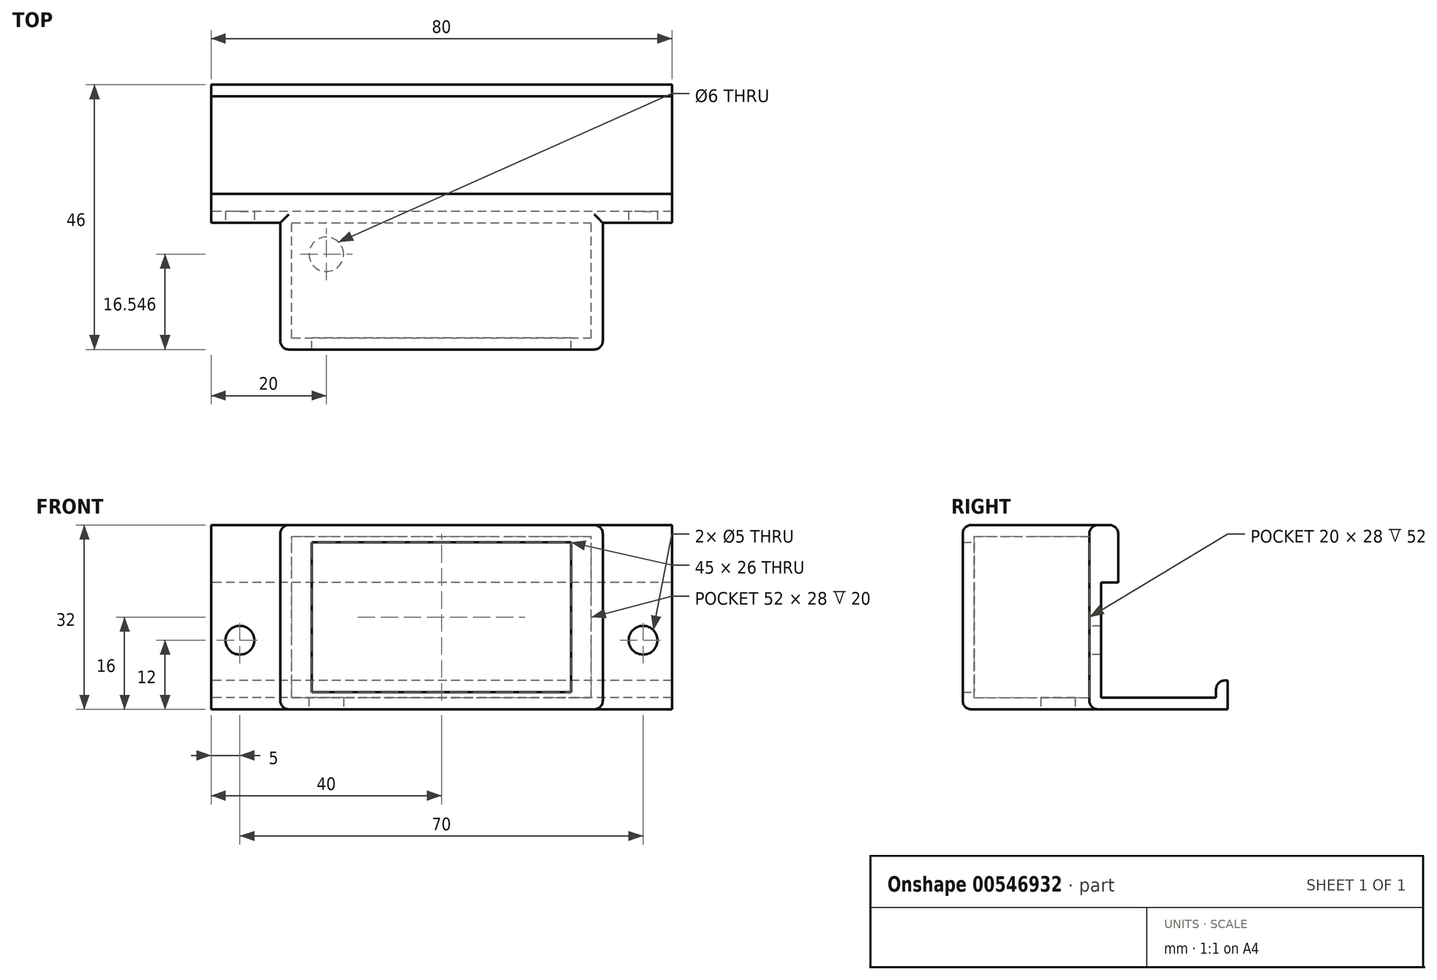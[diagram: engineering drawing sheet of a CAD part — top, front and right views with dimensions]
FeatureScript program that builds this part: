
annotation { "Feature Type Name" : "Feature", "Feature Type Description" : "" }
export const myFeature = defineFeature(function(context is Context, id is Id, definition is map)
    precondition{}
    {
        {
            var Q0;
            Q0=qCreatedBy(makeId("Right.planeOp"),FACE);
            var sketch = newSketch(context, id + "F0", { "sketchPlane" : qUnion([Q0])});
            skLineSegment(sketch, "E0", {"start": v(0, 0) * mm, "end": v(0, 32) * mm});
            skLineSegment(sketch, "E1", {"start": v(5, 32) * mm, "end": v(5, 22) * mm});
            skLineSegment(sketch, "E2", {"start": v(5, 22) * mm, "end": v(2, 22) * mm});
            skLineSegment(sketch, "E3", {"start": v(2, 22) * mm, "end": v(2, 2) * mm});
            skLineSegment(sketch, "E4", {"start": v(2, 2) * mm, "end": v(22, 2) * mm});
            skLineSegment(sketch, "E5", {"start": v(22, 2) * mm, "end": v(22, 5) * mm});
            skLineSegment(sketch, "E6", {"start": v(22, 5) * mm, "end": v(24, 5) * mm});
            skLineSegment(sketch, "E7", {"start": v(24, 5) * mm, "end": v(24, 0) * mm});
            skLineSegment(sketch, "E8", {"start": v(24, 0) * mm, "end": v(0, 0) * mm});
            skLineSegment(sketch, "E9.0", {"start": v(0, 32) * mm, "end": v(5, 32) * mm});
            skSolve(sketch);
        }
        {
            var Q0;
            Q0=makeQuery(id+"F0.imprint","IMPRINT",FACE,{"disambiguationData":[TD([[makeQuery(id+"F0.imprint","IMPRINT",EDGE,{"derivedFrom":sQuery(id+"F0.wireOp",EDGE,"E0")}),-1.0]])]});
            extrude(context, id + "F1", {"entities" : qUnion([Q0]), "depth" : 80 * mm, "offsetDistance" : 25 * mm});
        }
        {
            var Q0;
            Q0=qCreatedBy(makeId("Front.planeOp"),FACE);
            var sketch = newSketch(context, id + "F2", { "sketchPlane" : qUnion([Q0])});
            skLineSegment(sketch, "E10", {"start": v(0, 0) * mm, "end": v(0, 12) * mm, "construction": true});
            skLineSegment(sketch, "E11.0", {"start": v(5, 0) * mm, "end": v(5, 12) * mm, "construction": true});
            skCircle(sketch, "E12", {"center": v(5, 12) * mm, "radius": 2.5 * mm});
            skLineSegment(sketch, "E13", {"start": v(0, 0) * mm, "end": v(0, 16) * mm, "construction": true});
            skLineSegment(sketch, "E14", {"start": v(0, 0) * mm, "end": v(0, 32) * mm, "construction": true});
            skLineSegment(sketch, "E15", {"start": v(12, 32) * mm, "end": v(68, 32) * mm});
            skLineSegment(sketch, "E16", {"start": v(12, 0) * mm, "end": v(68, 0) * mm});
            skLineSegment(sketch, "E17", {"start": v(0, 12) * mm, "end": v(80, 12) * mm, "construction": true});
            skLineSegment(sketch, "E18", {"start": v(80, 12) * mm, "end": v(80, 0) * mm, "construction": true});
            skLineSegment(sketch, "E19.0", {"start": v(75, 12) * mm, "end": v(75, 0) * mm, "construction": true});
            skCircle(sketch, "E20", {"center": v(75, 12) * mm, "radius": 2.5 * mm});
            skLineSegment(sketch, "E21.0", {"start": v(40, 0) * mm, "end": v(40, 32) * mm, "construction": true});
            skLineSegment(sketch, "E22.0", {"start": v(68, 0) * mm, "end": v(68, 32) * mm});
            skLineSegment(sketch, "E23.0", {"start": v(12, 0) * mm, "end": v(12, 32) * mm});
            skLineSegment(sketch, "E24.0", {"start": v(14, 30) * mm, "end": v(66, 30) * mm});
            skLineSegment(sketch, "E25.0", {"start": v(14, 2) * mm, "end": v(66, 2) * mm});
            skLineSegment(sketch, "E26.0", {"start": v(14, 2) * mm, "end": v(14, 30) * mm});
            skLineSegment(sketch, "E27.0", {"start": v(66, 2) * mm, "end": v(66, 30) * mm});
            skSolve(sketch);
        }
        {
            var Q0;
            Q0=makeQuery(id+"F2.imprint","IMPRINT",FACE,{"disambiguationData":[TD([[makeQuery(id+"F2.imprint","IMPRINT",EDGE,{"derivedFrom":sQuery(id+"F2.wireOp",EDGE,"E12")}),1.0]])]});
            var Q1;
            Q1=makeQuery(id+"F2.imprint","IMPRINT",FACE,{"disambiguationData":[TD([[makeQuery(id+"F2.imprint","IMPRINT",EDGE,{"derivedFrom":sQuery(id+"F2.wireOp",EDGE,"E20")}),1.0]])]});
            extrude(context, id + "F3", {"entities" : qUnion([Q0, Q1]), "operationType" : NewBodyOperationType.REMOVE, "oppositeDirection" : true, "depth" : 10 * mm, "offsetDistance" : 25 * mm});
        }
        {
            var Q0;
            Q0=makeQuery(id+"F2.imprint","IMPRINT",FACE,{"disambiguationData":[TD([[makeQuery(id+"F2.imprint","IMPRINT",EDGE,{"derivedFrom":sQuery(id+"F2.wireOp",EDGE,"E15")}),-1.0]])]});
            extrude(context, id + "F4", {"entities" : qUnion([Q0]), "operationType" : NewBodyOperationType.ADD, "depth" : 20 * mm, "offsetDistance" : 25 * mm});
        }
        {
            var Q0;
            Q0=qCreatedBy(makeId("Front.planeOp"),FACE);
            cPlane(context, id + "F5", {"entities" : qUnion([Q0]), "cplaneType" : CPlaneType.OFFSET, "offset" : 20 * mm, "width" : 150 * mm, "height" : 150 * mm});
        }
        {
            var Q0;
            Q0=qCreatedBy(id+"F5.planeOp",FACE);
            var sketch = newSketch(context, id + "F6", { "sketchPlane" : qUnion([Q0])});
            skLineSegment(sketch, "E28", {"start": v(12, 0) * mm, "end": v(68, 0) * mm});
            skLineSegment(sketch, "E29", {"start": v(68, 0) * mm, "end": v(68, 32) * mm});
            skLineSegment(sketch, "E30", {"start": v(68, 32) * mm, "end": v(12, 32) * mm});
            skLineSegment(sketch, "E31", {"start": v(12, 32) * mm, "end": v(12, 0) * mm});
            skLineSegment(sketch, "E32.0", {"start": v(62.5, 29) * mm, "end": v(17.5, 29) * mm});
            skLineSegment(sketch, "E33.0", {"start": v(17.5, 3) * mm, "end": v(62.5, 3) * mm});
            skLineSegment(sketch, "E34.0", {"start": v(17.5, 29) * mm, "end": v(17.5, 3) * mm});
            skLineSegment(sketch, "E35.0", {"start": v(62.5, 3) * mm, "end": v(62.5, 29) * mm});
            skSolve(sketch);
        }
        {
            var Q0;
            Q0=makeQuery(id+"F6.imprint","IMPRINT",FACE,{"disambiguationData":[TD([[makeQuery(id+"F6.imprint","IMPRINT",EDGE,{"derivedFrom":sQuery(id+"F6.wireOp",EDGE,"E28")}),1.0]])]});
            extrude(context, id + "F7", {"entities" : qUnion([Q0]), "operationType" : NewBodyOperationType.ADD, "depth" : 2 * mm, "offsetDistance" : 25 * mm});
        }
        {
            var Q0;
            Q0=makeQuery(id+"F7.opExtrude","CAP_EDGE",EDGE,{"disambiguationData":[OSD([sQuery(id+"F6.wireOp",EDGE,"E29")])],"isStart":false});
            var Q1;
            Q1=makeQuery(id+"F7.opExtrude","CAP_EDGE",EDGE,{"disambiguationData":[OSD([sQuery(id+"F6.wireOp",EDGE,"E30")])],"isStart":false});
            var Q2;
            Q2=makeQuery(id+"F7.opExtrude","CAP_EDGE",EDGE,{"disambiguationData":[OSD([sQuery(id+"F6.wireOp",EDGE,"E31")])],"isStart":false});
            var Q3;
            Q3=makeQuery(id+"F7.opExtrude","CAP_EDGE",EDGE,{"disambiguationData":[OSD([sQuery(id+"F6.wireOp",EDGE,"E28")])],"isStart":false});
            var Q4;
            Q4=makeQuery(id+"F7.boolean.opBoolean","MERGE",EDGE,{"derivedFrom":[makeQuery(id+"F4.opExtrude","SWEPT_EDGE",EDGE,{"disambiguationData":[OSD([sQuery(id+"F2.wireOp",EDGE,"E15"),sQuery(id+"F2.wireOp",EDGE,"E22.0")])]}),makeQuery(id+"F7.opExtrude","SWEPT_EDGE",EDGE,{"disambiguationData":[OSD([sQuery(id+"F6.wireOp",EDGE,"E29"),sQuery(id+"F6.wireOp",EDGE,"E30")])]})]});
            var Q5;
            Q5=makeQuery(id+"F7.boolean.opBoolean","MERGE",EDGE,{"derivedFrom":[makeQuery(id+"F4.opExtrude","SWEPT_EDGE",EDGE,{"disambiguationData":[OSD([sQuery(id+"F2.wireOp",EDGE,"E15"),sQuery(id+"F2.wireOp",EDGE,"E23.0")])]}),makeQuery(id+"F7.opExtrude","SWEPT_EDGE",EDGE,{"disambiguationData":[OSD([sQuery(id+"F6.wireOp",EDGE,"E30"),sQuery(id+"F6.wireOp",EDGE,"E31")])]})]});
            var Q6;
            Q6=makeQuery(id+"F7.boolean.opBoolean","MERGE",EDGE,{"derivedFrom":[makeQuery(id+"F4.opExtrude","SWEPT_EDGE",EDGE,{"disambiguationData":[OSD([sQuery(id+"F2.wireOp",EDGE,"E16"),sQuery(id+"F2.wireOp",EDGE,"E23.0")])]}),makeQuery(id+"F7.opExtrude","SWEPT_EDGE",EDGE,{"disambiguationData":[OSD([sQuery(id+"F6.wireOp",EDGE,"E28"),sQuery(id+"F6.wireOp",EDGE,"E31")])]})]});
            var Q7;
            Q7=makeQuery(id+"F7.boolean.opBoolean","MERGE",EDGE,{"derivedFrom":[makeQuery(id+"F4.opExtrude","SWEPT_EDGE",EDGE,{"disambiguationData":[OSD([sQuery(id+"F2.wireOp",EDGE,"E16"),sQuery(id+"F2.wireOp",EDGE,"E22.0")])]}),makeQuery(id+"F7.opExtrude","SWEPT_EDGE",EDGE,{"disambiguationData":[OSD([sQuery(id+"F6.wireOp",EDGE,"E28"),sQuery(id+"F6.wireOp",EDGE,"E29")])]})]});
            var Q8;
            Q8=makeQuery(id+"F1.opExtrude","SWEPT_EDGE",EDGE,{"disambiguationData":[OSD([sQuery(id+"F0.wireOp",EDGE,"E5"),sQuery(id+"F0.wireOp",EDGE,"E6")])]});
            var Q9;
            Q9=makeQuery(id+"F1.opExtrude","SWEPT_EDGE",EDGE,{"disambiguationData":[OSD([sQuery(id+"F0.wireOp",EDGE,"E1"),sQuery(id+"F0.wireOp",EDGE,"E9.0")])]});
            var Q10;
            {var subQ0=sQuery(id+"F0.wireOp",EDGE,"E9.0");var subQ1=sQuery(id+"F0.wireOp",EDGE,"E0");Q10=makeQuery(id+"F4.boolean.opBoolean","SPLIT",EDGE,{"disambiguationData":[TD([makeQuery(id+"F4.opExtrude","SWEPT_FACE",FACE,{"disambiguationData":[OSD([sQuery(id+"F2.wireOp",EDGE,"E22.0")])]})])],"derivedFrom":makeQuery(id+"F1.opExtrude","SWEPT_EDGE",EDGE,{"disambiguationData":[OSD([subQ1,subQ0])]})});}
            var Q11;
            {var subQ0=sQuery(id+"F0.wireOp",EDGE,"E9.0");var subQ1=sQuery(id+"F0.wireOp",EDGE,"E0");Q11=makeQuery(id+"F4.boolean.opBoolean","SPLIT",EDGE,{"disambiguationData":[TD([makeQuery(id+"F4.opExtrude","SWEPT_FACE",FACE,{"disambiguationData":[OSD([sQuery(id+"F2.wireOp",EDGE,"E23.0")])]})])],"derivedFrom":makeQuery(id+"F1.opExtrude","SWEPT_EDGE",EDGE,{"disambiguationData":[OSD([subQ1,subQ0])]})});}
            var Q12;
            {var subQ0=sQuery(id+"F0.wireOp",EDGE,"E8");var subQ1=sQuery(id+"F0.wireOp",EDGE,"E0");Q12=makeQuery(id+"F4.boolean.opBoolean","SPLIT",EDGE,{"disambiguationData":[TD([makeQuery(id+"F4.opExtrude","SWEPT_FACE",FACE,{"disambiguationData":[OSD([sQuery(id+"F2.wireOp",EDGE,"E22.0")])]})])],"derivedFrom":makeQuery(id+"F1.opExtrude","SWEPT_EDGE",EDGE,{"disambiguationData":[OSD([subQ1,subQ0])]})});}
            var Q13;
            {var subQ0=sQuery(id+"F0.wireOp",EDGE,"E8");var subQ1=sQuery(id+"F0.wireOp",EDGE,"E0");Q13=makeQuery(id+"F4.boolean.opBoolean","SPLIT",EDGE,{"disambiguationData":[TD([makeQuery(id+"F4.opExtrude","SWEPT_FACE",FACE,{"disambiguationData":[OSD([sQuery(id+"F2.wireOp",EDGE,"E23.0")])]})])],"derivedFrom":makeQuery(id+"F1.opExtrude","SWEPT_EDGE",EDGE,{"disambiguationData":[OSD([subQ1,subQ0])]})});}
            fillet(context, id + "F8", {"entities" : qUnion([Q0, Q1, Q2, Q3, Q4, Q5, Q6, Q7, Q8, Q9, Q10, Q11, Q12, Q13]), "radius" : 1.5 * mm, "tangentPropagation" : true, "allowEdgeOverflow" : false});
        }
        {
            var Q0;
            Q0=qCreatedBy(makeId("Top.planeOp"),FACE);
            var sketch = newSketch(context, id + "F9", { "sketchPlane" : qUnion([Q0])});
            skLineSegment(sketch, "E36", {"start": v(0, 0) * mm, "end": v(20, 0) * mm, "construction": true});
            skLineSegment(sketch, "E37", {"start": v(20, 0) * mm, "end": v(20, -5.45) * mm, "construction": true});
            skCircle(sketch, "E38", {"center": v(20, -5.45) * mm, "radius": 3 * mm});
            skSolve(sketch);
        }
        {
            var Q0;
            Q0=makeQuery(id+"F9.imprint","IMPRINT",FACE,{"disambiguationData":[TD([[makeQuery(id+"F9.imprint","IMPRINT",EDGE,{"derivedFrom":sQuery(id+"F9.wireOp",EDGE,"E38")}),1.0]])]});
            extrude(context, id + "F10", {"entities" : qUnion([Q0]), "operationType" : NewBodyOperationType.REMOVE, "depth" : 10 * mm, "offsetDistance" : 25 * mm});
        }
    });
